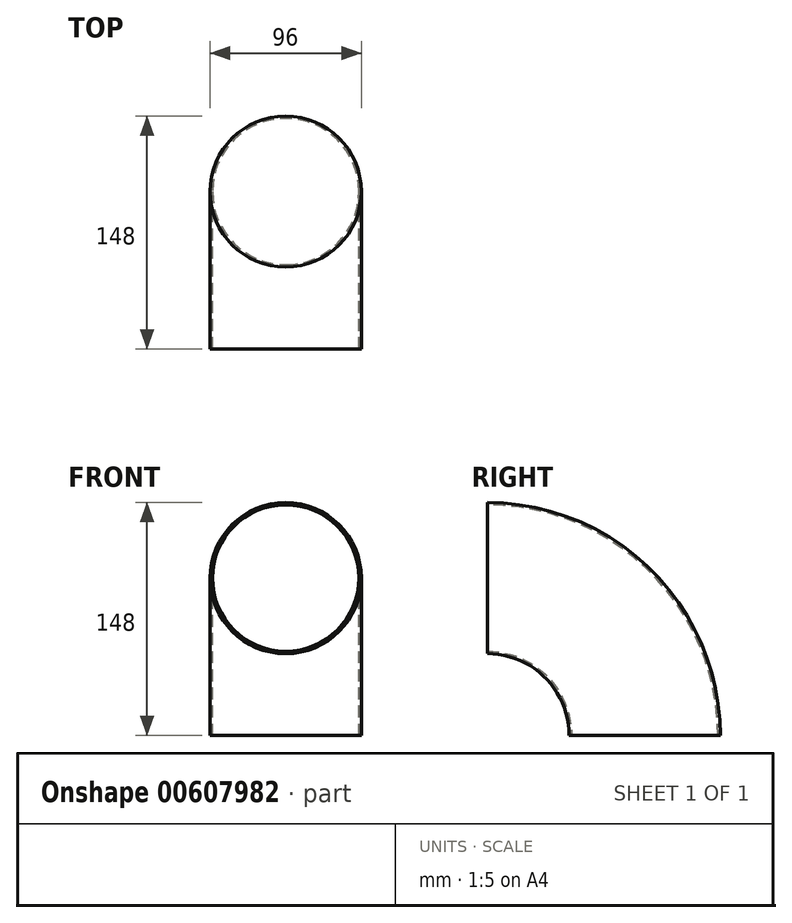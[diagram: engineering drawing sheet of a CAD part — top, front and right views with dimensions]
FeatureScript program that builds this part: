
annotation { "Feature Type Name" : "Feature", "Feature Type Description" : "" }
export const myFeature = defineFeature(function(context is Context, id is Id, definition is map)
    precondition{}
    {
        {
            var Q0;
            Q0=qCreatedBy(makeId("Front.planeOp"),FACE);
            var sketch = newSketch(context, id + "F0", { "sketchPlane" : qUnion([Q0])});
            skCircle(sketch, "E0", {"center": v(0, 0) * mm, "radius": 46.5 * mm});
            skCircle(sketch, "E1", {"center": v(0, 0) * mm, "radius": 48 * mm});
            skSolve(sketch);
        }
        {
            var Q0;
            Q0=qCreatedBy(makeId("Right.planeOp"),FACE);
            var sketch = newSketch(context, id + "F1", { "sketchPlane" : qUnion([Q0])});
            skPoint(sketch, "E2", {"position": v(0, -100) * mm});
            skLineSegment(sketch, "E3", {"start": v(0, -100) * mm, "end": v(181.49, -100) * mm, "construction": true});
            skArc(sketch, "E4", {"start": v(0, 0) * mm, "mid": v(70.71, -29.29) * mm, "end": v(100, -100) * mm});
            skSolve(sketch);
        }
        {
            var Q0;
            Q0=makeQuery(id+"F0.imprint","IMPRINT",FACE,{"disambiguationData":[TD([[makeQuery(id+"F0.imprint","IMPRINT",EDGE,{"derivedFrom":sQuery(id+"F0.wireOp",EDGE,"E0")}),-1.0]])]});
            var Q1;
            Q1=sQuery(id+"F1.wireOp",EDGE,"E4");
            sweep(context, id + "F2", {"profiles" : qUnion([Q0]), "path" : qUnion([Q1])});
        }
    });
